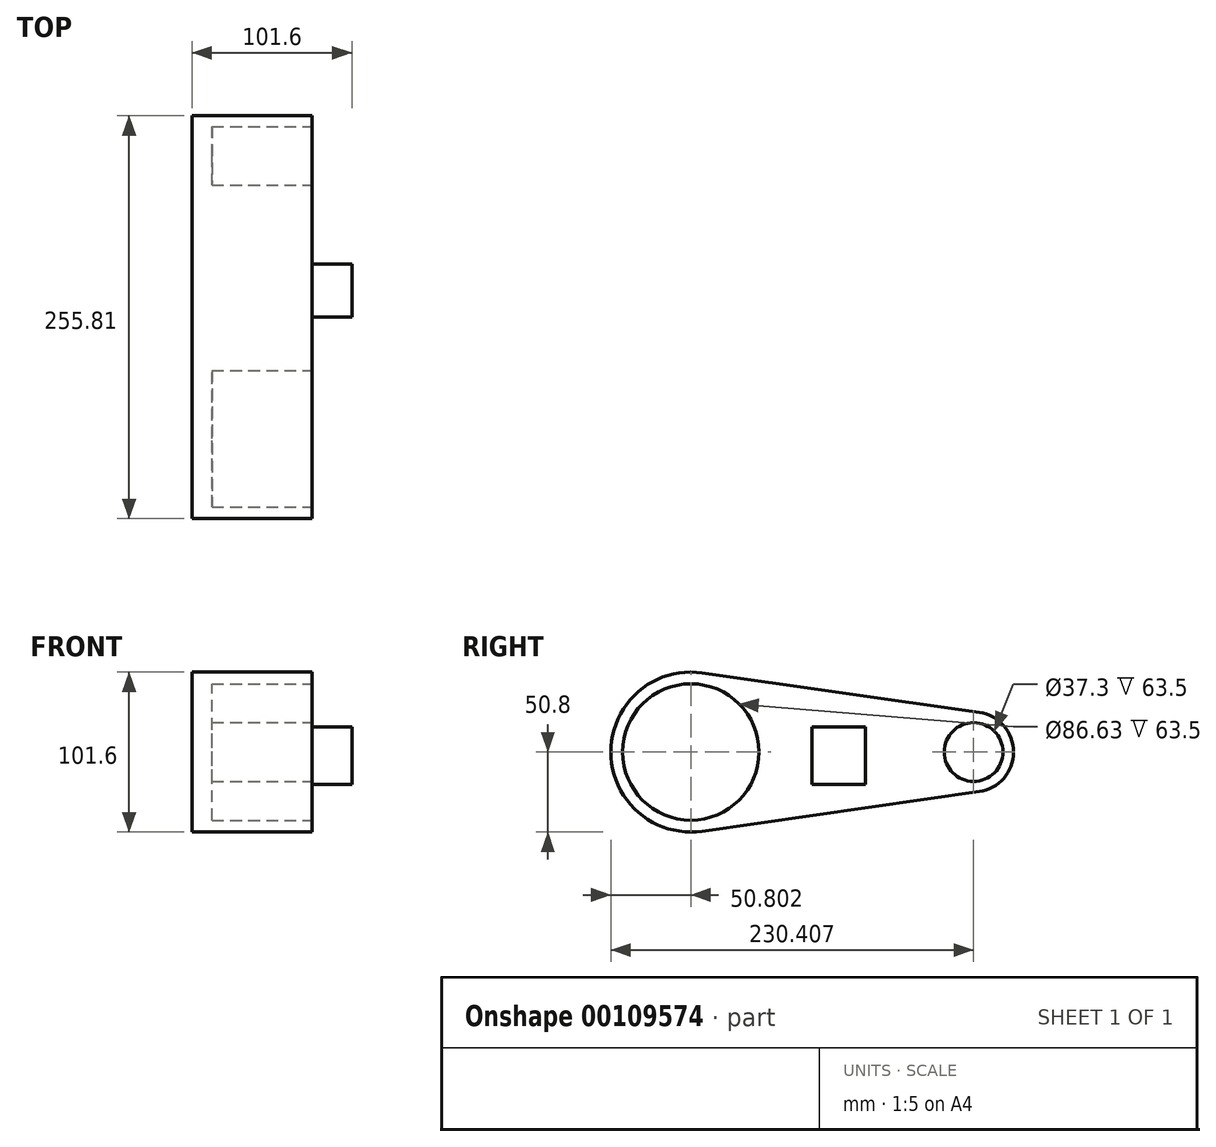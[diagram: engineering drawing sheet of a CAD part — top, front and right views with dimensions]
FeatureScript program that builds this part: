
annotation { "Feature Type Name" : "Feature", "Feature Type Description" : "" }
export const myFeature = defineFeature(function(context is Context, id is Id, definition is map)
    precondition{}
    {
        {
            var Q0;
            Q0=qCreatedBy(makeId("Right.planeOp"),FACE);
            var sketch = newSketch(context, id + "F0", { "sketchPlane" : qUnion([Q0])});
            skCircle(sketch, "E0", {"center": v(-115.25, 0) * mm, "radius": 50.8 * mm});
            skCircle(sketch, "E1", {"center": v(64.36, 0) * mm, "radius": 25.4 * mm});
            skLineSegment(sketch, "E2", {"start": v(-108.06, 50.29) * mm, "end": v(67.95, 25.14) * mm});
            skLineSegment(sketch, "E3", {"start": v(-108.06, -50.29) * mm, "end": v(67.95, -25.14) * mm});
            skSolve(sketch);
        }
        {
            var Q0;
            Q0 = qSketchRegion(id + "F0", true);
            extrude(context, id + "F1", {"entities" : qUnion([Q0]), "depth" : 76.2 * mm});
        }
        {
            var Q0;
            Q0=makeQuery(id+"F1.opExtrude","CAP_FACE",FACE,{"disambiguationData":[OSD([sQuery(id+"F0.wireOp",EDGE,"E0"),sQuery(id+"F0.wireOp",EDGE,"E1"),sQuery(id+"F0.wireOp",EDGE,"E2"),sQuery(id+"F0.wireOp",EDGE,"E3")])],"isStart":false});
            var sketch = newSketch(context, id + "F2", { "sketchPlane" : qUnion([Q0])});
            skCircle(sketch, "E4", {"center": v(-115.25, 0) * mm, "radius": 43.31 * mm});
            skCircle(sketch, "E5", {"center": v(64.36, 0) * mm, "radius": 18.65 * mm});
            skSolve(sketch);
        }
        {
            var Q0;
            Q0 = qSketchRegion(id + "F2", true);
            extrude(context, id + "F3", {"entities" : qUnion([Q0]), "operationType" : NewBodyOperationType.REMOVE, "oppositeDirection" : true, "depth" : 63.5 * mm});
        }
        {
            var Q0;
            Q0=makeQuery(id+"F1.opExtrude","CAP_FACE",FACE,{"disambiguationData":[OSD([sQuery(id+"F0.wireOp",EDGE,"E0"),sQuery(id+"F0.wireOp",EDGE,"E1"),sQuery(id+"F0.wireOp",EDGE,"E2"),sQuery(id+"F0.wireOp",EDGE,"E3")])],"isStart":false});
            var sketch = newSketch(context, id + "F4", { "sketchPlane" : qUnion([Q0])});
            skLineSegment(sketch, "E6.bottom", {"start": v(-38.16, 16.02) * mm, "end": v(-4.4, 16.02) * mm});
            skLineSegment(sketch, "E6.top", {"start": v(-38.16, -20.52) * mm, "end": v(-4.4, -20.52) * mm});
            skLineSegment(sketch, "E6.left", {"start": v(-38.16, 16.02) * mm, "end": v(-38.16, -20.52) * mm});
            skLineSegment(sketch, "E6.right", {"start": v(-4.4, 16.02) * mm, "end": v(-4.4, -20.52) * mm});
            skSolve(sketch);
        }
        {
            var Q0;
            Q0=makeQuery(id+"F4.imprint","IMPRINT",FACE,{"disambiguationData":[TD([[makeQuery(id+"F4.imprint","IMPRINT",EDGE,{"derivedFrom":sQuery(id+"F4.wireOp",EDGE,"E6.bottom")}),-1.0]])]});
            extrude(context, id + "F5", {"entities" : qUnion([Q0]), "operationType" : NewBodyOperationType.ADD, "depth" : 25.4 * mm});
        }
    });
